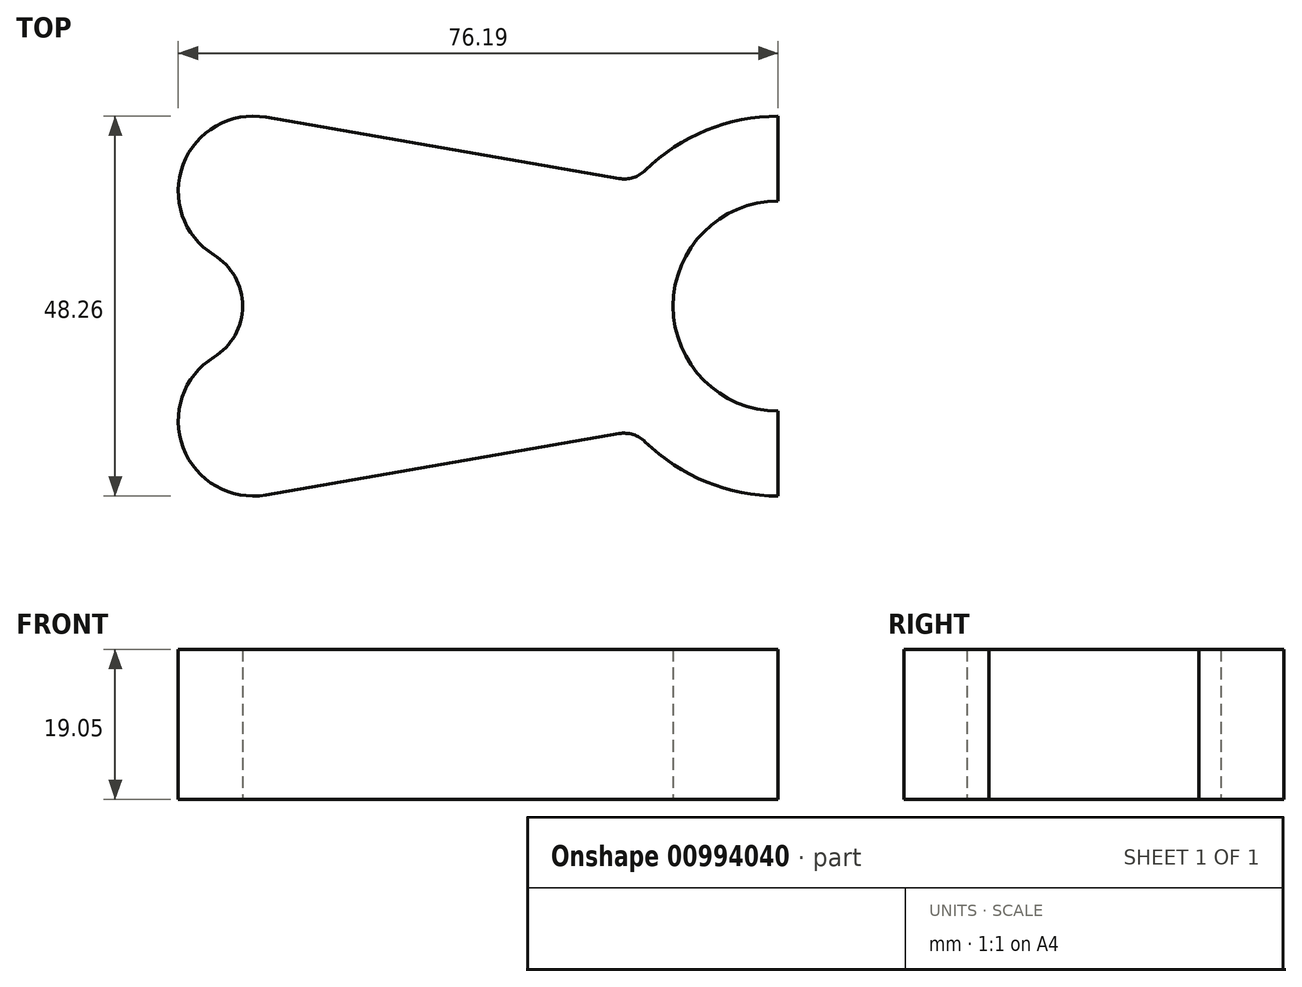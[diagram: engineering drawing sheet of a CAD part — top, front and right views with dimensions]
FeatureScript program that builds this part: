
annotation { "Feature Type Name" : "Feature", "Feature Type Description" : "" }
export const myFeature = defineFeature(function(context is Context, id is Id, definition is map)
    precondition{}
    {
        {
            var Q0;
            Q0=qCreatedBy(makeId("Top.planeOp"),FACE);
            var sketch = newSketch(context, id + "F0", { "sketchPlane" : qUnion([Q0])});
            skArc(sketch, "E0", {"start": v(1.63, 9.38) * mm, "mid": v(-8.9, 3.37) * mm, "end": v(-4.99, -8.11) * mm});
            skLineSegment(sketch, "E1", {"start": v(0, 0) * mm, "end": v(0, -29.21) * mm});
            skArc(sketch, "E2", {"start": v(-4.99, -21.1) * mm, "mid": v(-8.9, -32.58) * mm, "end": v(1.63, -38.6) * mm});
            skLineSegment(sketch, "E3", {"start": v(0, -14.6) * mm, "end": v(113.9, -14.6) * mm, "construction": true});
            skLineSegment(sketch, "E4.0", {"start": v(66.68, 22.87) * mm, "end": v(66.68, -46.37) * mm});
            skArc(sketch, "E5.MirrorC", {"start": v(131.72, 9.38) * mm, "mid": v(142.26, 3.37) * mm, "end": v(138.34, -8.11) * mm});
            skArc(sketch, "E6.MirrorC", {"start": v(138.34, -21.1) * mm, "mid": v(142.26, -32.58) * mm, "end": v(131.72, -38.6) * mm});
            skCircle(sketch, "E7", {"center": v(66.68, -14.6) * mm, "radius": 12.7 * mm});
            skCircle(sketch, "E8", {"center": v(66.68, -14.6) * mm, "radius": 13.33 * mm});
            skArc(sketch, "E9", {"start": v(49.8, -31.84) * mm, "mid": v(66.68, -38.73) * mm, "end": v(83.56, -31.84) * mm});
            skLineSegment(sketch, "E10", {"start": v(66.68, -1.9) * mm, "end": v(64.27, -1.49) * mm});
            skLineSegment(sketch, "E11.MirrorCS", {"start": v(66.68, -27.3) * mm, "end": v(64.27, -27.72) * mm});
            skLineSegment(sketch, "E12.trimOffspring", {"start": v(46.47, 1.6) * mm, "end": v(0, 9.67) * mm});
            skLineSegment(sketch, "E13.trimOffspring", {"start": v(46.47, -30.81) * mm, "end": v(0, -38.88) * mm});
            skArc(sketch, "E14", {"start": v(46.47, 1.6) * mm, "mid": v(48.26, 1.72) * mm, "end": v(49.8, 2.63) * mm});
            skArc(sketch, "E15.MirrorCS", {"start": v(46.47, -30.81) * mm, "mid": v(48.26, -30.93) * mm, "end": v(49.8, -31.84) * mm});
            skArc(sketch, "E16", {"start": v(-4.99, -21.1) * mm, "mid": v(-1.36, -14.6) * mm, "end": v(-4.99, -8.11) * mm});
            skArc(sketch, "E17.MirrorCS", {"start": v(86.88, 1.6) * mm, "mid": v(85.1, 1.72) * mm, "end": v(83.56, 2.63) * mm});
            skLineSegment(sketch, "E18.MirrorCS", {"start": v(86.88, 1.6) * mm, "end": v(133.35, 9.67) * mm});
            skArc(sketch, "E19.MirrorCS", {"start": v(138.34, -21.1) * mm, "mid": v(134.71, -14.6) * mm, "end": v(138.34, -8.11) * mm});
            skLineSegment(sketch, "E20.MirrorCS", {"start": v(86.88, -30.81) * mm, "end": v(133.35, -38.88) * mm});
            skArc(sketch, "E21.MirrorCS", {"start": v(86.88, -30.81) * mm, "mid": v(85.1, -30.93) * mm, "end": v(83.56, -31.84) * mm});
            skArc(sketch, "E22.trimOffspring", {"start": v(83.56, 2.63) * mm, "mid": v(66.68, 9.53) * mm, "end": v(49.8, 2.63) * mm});
            skSolve(sketch);
        }
        {
            var Q0;
            {var subQ3=sQuery(id+"F0.wireOp",EDGE,"E17.MirrorCS");Q0=makeQuery(id+"F0.imprint","IMPRINT",FACE,{"disambiguationData":[TD([[makeQuery(id+"F0.imprint","IMPRINT",EDGE,{"derivedFrom":subQ3}),1.0]])]});}
            var Q1;
            {var subQ9=sQuery(id+"F0.wireOp",EDGE,"E0");Q1=makeQuery(id+"F0.imprint","IMPRINT",FACE,{"disambiguationData":[TD([[makeQuery(id+"F0.imprint","IMPRINT",EDGE,{"derivedFrom":subQ9}),1.0]])]});}
            extrude(context, id + "F1", {"entities" : qUnion([Q0, Q1]), "depth" : 19.05 * mm, "offsetDistance" : 25.4 * mm});
        }
    });
